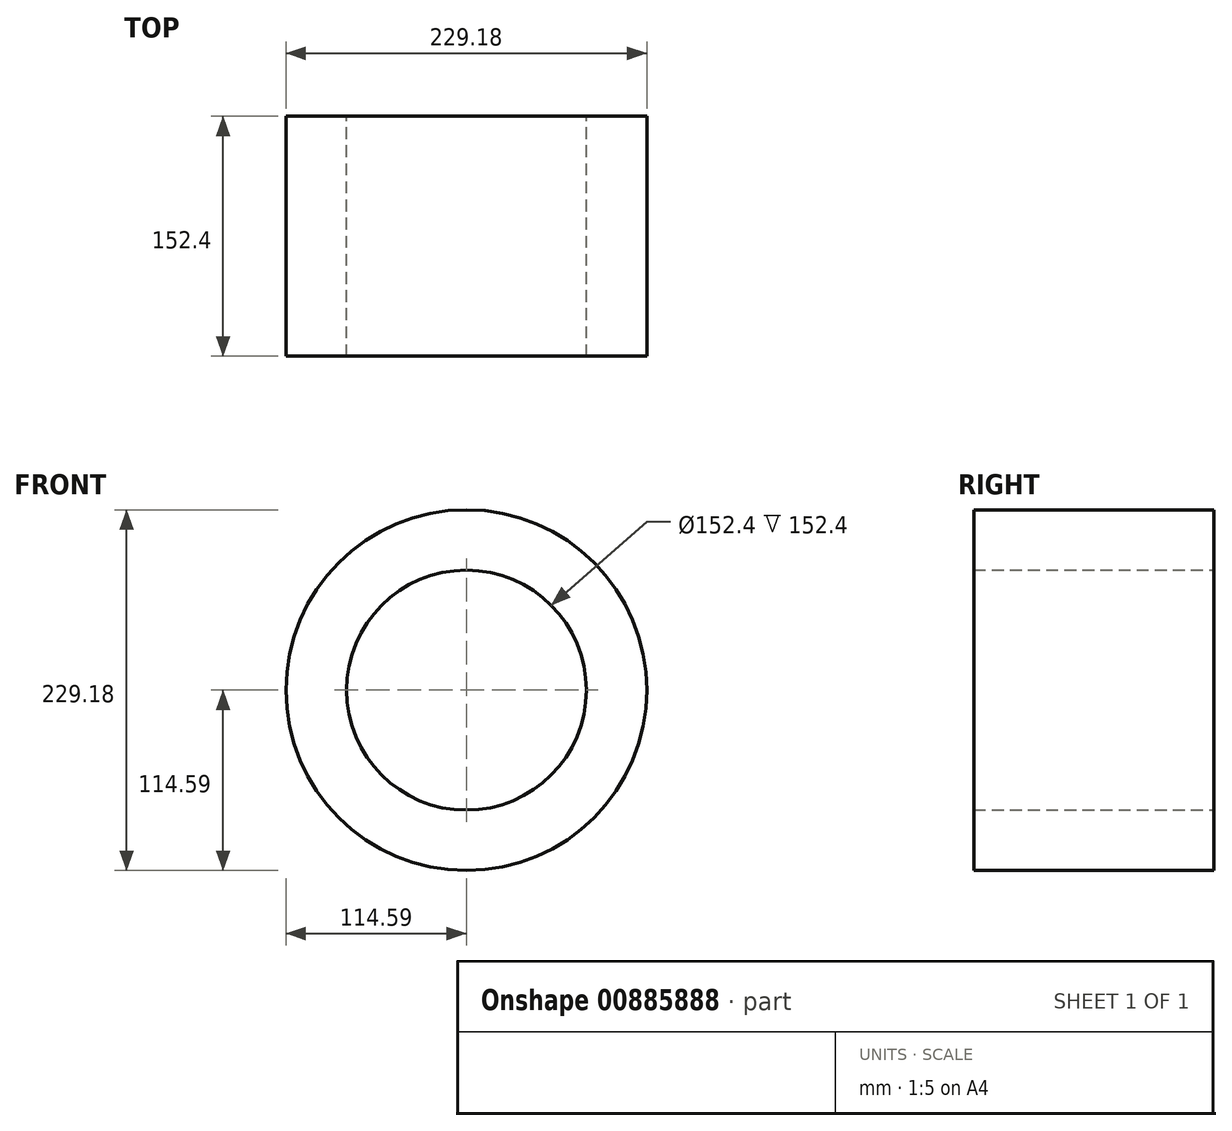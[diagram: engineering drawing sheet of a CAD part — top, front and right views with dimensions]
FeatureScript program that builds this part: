
annotation { "Feature Type Name" : "Feature", "Feature Type Description" : "" }
export const myFeature = defineFeature(function(context is Context, id is Id, definition is map)
    precondition{}
    {
        {
            var Q0;
            Q0=qCreatedBy(makeId("Front.planeOp"),FACE);
            var sketch = newSketch(context, id + "F0", { "sketchPlane" : qUnion([Q0])});
            skCircle(sketch, "E0", {"center": v(0, 0) * mm, "radius": 114.59 * mm});
            skSolve(sketch);
        }
        {
            var Q0;
            Q0=makeQuery(id+"F0.imprint","IMPRINT",FACE,{"disambiguationData":[TD([[makeQuery(id+"F0.imprint","IMPRINT",EDGE,{"derivedFrom":sQuery(id+"F0.wireOp",EDGE,"E0")}),1.0]])]});
            extrude(context, id + "F1", {"entities" : qUnion([Q0]), "depth" : 152.4 * mm, "offsetDistance" : 25.4 * mm});
        }
        {
            var Q0;
            Q0=makeQuery(id+"F1.opExtrude","CAP_FACE",FACE,{"disambiguationData":[OSD([sQuery(id+"F0.wireOp",EDGE,"E0")])],"isStart":true});
            var sketch = newSketch(context, id + "F2", { "sketchPlane" : qUnion([Q0])});
            skPoint(sketch, "E1", {"position": v(0, 0) * mm});
            skSolve(sketch);
        }
        {
            var Q0;
            Q0=sQuery(id+"F2.wireOp",VERTEX,"E1");
            var Q1;
            Q1=makeQuery(id+"F1.opExtrude","SWEPT_BODY",BODY,{"disambiguationData":[OSD([sQuery(id+"F0.wireOp",EDGE,"E0")])]});
            hole(context, id + "F3", {"style" : HoleStyle.SIMPLE, "endStyle" : HoleEndStyle.THROUGH, "holeDiameter" : 152.4 * mm, "majorDiameter" : 6.35 * mm, "isTappedThrough" : true, "tappedDepth" : 12.7 * mm, "tapClearance" : 3, "locations" : qUnion([Q0]), "scope" : qUnion([Q1])});
        }
    });
